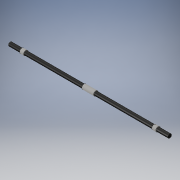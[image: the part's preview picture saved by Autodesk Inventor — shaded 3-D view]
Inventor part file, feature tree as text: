
AUTODESK INVENTOR PART (.ipt)
format: ipt  version: 2019 (Build 230136000, 136)  size: 121,344 bytes
history: native  units: in
note: dims shown in document units (in); Inventor stores cm internally (conversion verified against a paired STEP export)
features: extrude x4, sketch x4, plane x3
ambient origin geometry x8: Origin, YZ Plane, XZ Plane, XY Plane, X Axis, Y Axis, Z Axis, Center Point
bodies: Solid1 (feature_tree)
feature tree (11):
  extrude  "Extrusion1"  Depth=8.0709in TaperAngle=0.0deg
  plane  "Work Plane1"
  extrude  "Extrusion2"  Depth=0.2362in
  plane  "Work Plane2"
  extrude  "Extrusion3"  [1 undecoded]
  plane  "Work Plane3"
  extrude  "Extrusion4"  Depth=0.1969in TaperAngle=0.0deg
  sketch  "Sketch1"  dims[d0=0.1969in d1=8.0709in d2=0.0in]
  sketch  "Sketch2"  dims[d3=-0.7874in d4=0.2362in]
  sketch  "Sketch3"  dims[d5=0.1969in d6=0.0in d7=-0.7874in]
  sketch  "Sketch4"  dims[d8=0.2362in d9=0.1969in d10=0.0in d11=0.2362in d12=0.5906in d13=0.0in]
note: 1 required parameter value undecoded (feature->parameter linkage not recoverable at this tier; creation-order binding heuristic only, values carry confidence <= 0.55)
